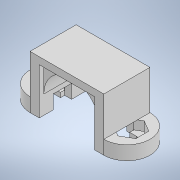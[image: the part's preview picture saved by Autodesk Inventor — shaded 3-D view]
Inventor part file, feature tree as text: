
AUTODESK INVENTOR PART (.ipt)
format: ipt  version: 2020 (Build 240168000, 168)  size: 229,376 bytes
history: native  units: mm
features: sketch x5, extrude x4, other x2, hole x1, fillet x1
ambient origin geometry x8: Origin, YZ Plane, XZ Plane, XY Plane, X Axis, Y Axis, Z Axis, Center Point
bodies: Body1 (feature_tree)
feature tree (13):
  other  "Кронштейн для двигателей серии N"
  other  "Твердое тело1"
  extrude  "Выдавливание1"  Depth=12.0mm
  hole  "Отверстие2"  [1 undecoded]
  extrude  "Выдавливание2"  Depth=4.0mm
  fillet  "Сопряжение1"  Radius=2.0mm
  extrude  "Выдавливание4"  Depth=2.0mm
  extrude  "Выдавливание5"  Depth=2.5mm
  sketch  "Эскиз1"
  sketch  "Эскиз2"
  sketch  "Эскиз3"
  sketch  "Эскиз5"
  sketch  "Эскиз6"
note: 1 required parameter value undecoded (feature->parameter linkage not recoverable at this tier; creation-order binding heuristic only, values carry confidence <= 0.55)
